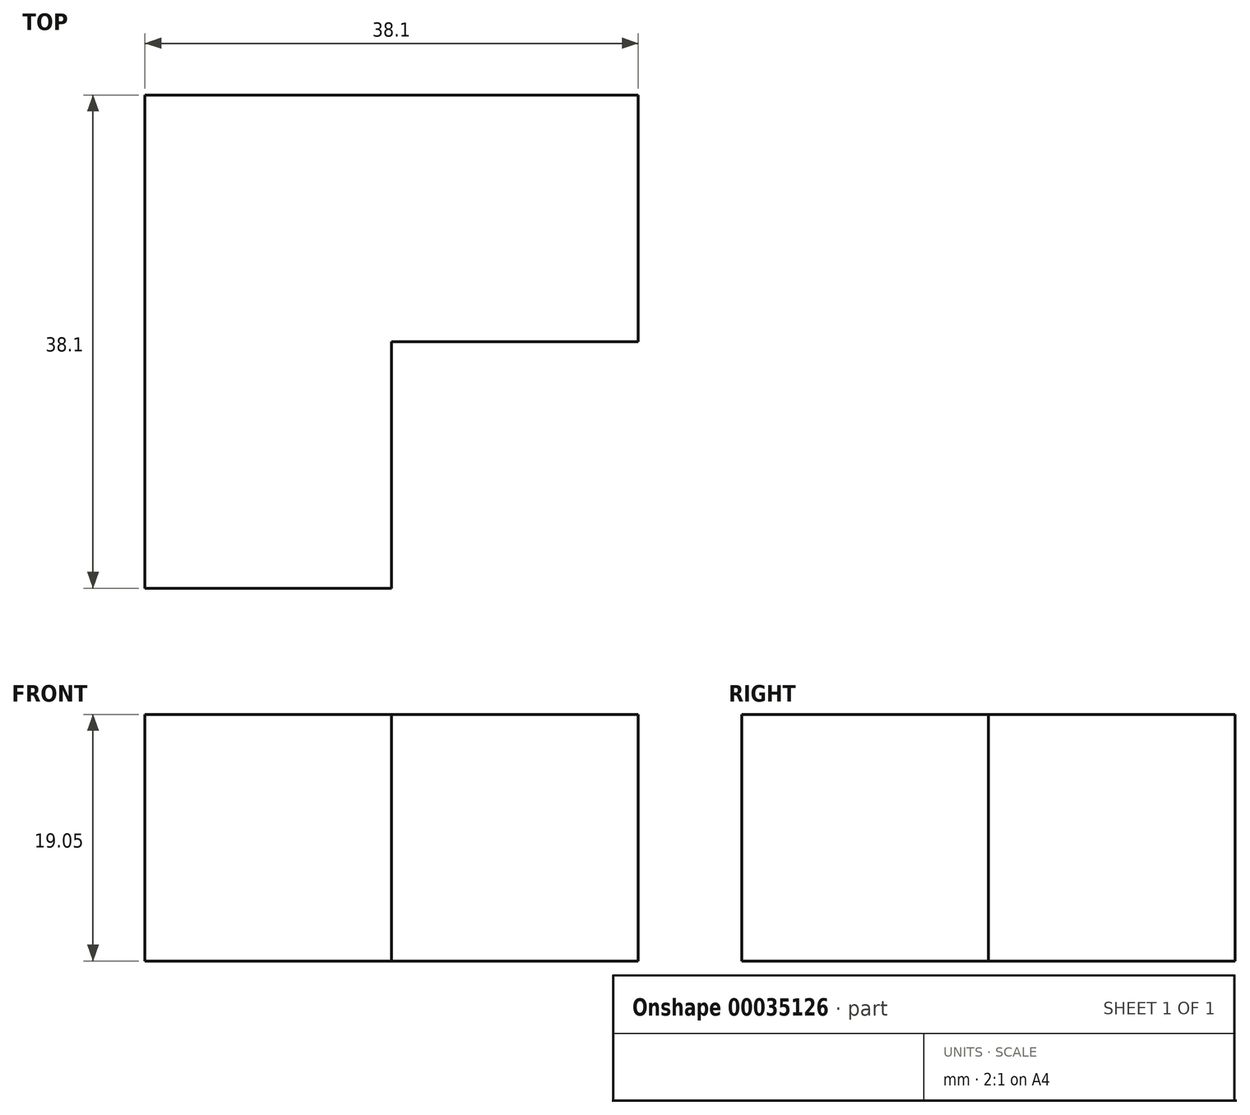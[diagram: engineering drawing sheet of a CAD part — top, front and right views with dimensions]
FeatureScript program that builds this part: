
annotation { "Feature Type Name" : "Feature", "Feature Type Description" : "" }
export const myFeature = defineFeature(function(context is Context, id is Id, definition is map)
    precondition{}
    {
        {
            var Q0;
            Q0=qCreatedBy(makeId("Top.planeOp"),FACE);
            var sketch = newSketch(context, id + "F0", { "sketchPlane" : qUnion([Q0])});
            skLineSegment(sketch, "E0.bottom", {"start": v(0, 0) * mm, "end": v(19.05, 0) * mm});
            skLineSegment(sketch, "E0.top", {"start": v(0, -19.05) * mm, "end": v(19.05, -19.05) * mm});
            skLineSegment(sketch, "E0.left", {"start": v(0, 0) * mm, "end": v(0, -19.05) * mm});
            skLineSegment(sketch, "E0.right", {"start": v(19.05, 0) * mm, "end": v(19.05, -19.05) * mm});
            skSolve(sketch);
        }
        {
            var Q0;
            Q0=makeQuery(id+"F0.imprint","IMPRINT",FACE,{"disambiguationData":[TD([[makeQuery(id+"F0.imprint","IMPRINT",EDGE,{"derivedFrom":sQuery(id+"F0.wireOp",EDGE,"E0.bottom")}),-1.0]])]});
            extrude(context, id + "F1", {"entities" : qUnion([Q0]), "depth" : 19.05 * mm});
        }
        {
            var Q0;
            Q0=makeQuery(id+"F1.opExtrude","SWEPT_FACE",FACE,{"disambiguationData":[OSD([sQuery(id+"F0.wireOp",EDGE,"E0.top")])]});
            var sketch = newSketch(context, id + "F2", { "sketchPlane" : qUnion([Q0])});
            skLineSegment(sketch, "E1.bottom", {"start": v(0, 19.05) * mm, "end": v(19.05, 19.05) * mm});
            skLineSegment(sketch, "E1.top", {"start": v(0, 0) * mm, "end": v(19.05, 0) * mm});
            skLineSegment(sketch, "E1.left", {"start": v(0, 19.05) * mm, "end": v(0, 0) * mm});
            skLineSegment(sketch, "E1.right", {"start": v(19.05, 19.05) * mm, "end": v(19.05, 0) * mm});
            skSolve(sketch);
        }
        {
            var Q0;
            Q0=makeQuery(id+"F2.imprint","IMPRINT",FACE,{"disambiguationData":[TD([[makeQuery(id+"F2.imprint","IMPRINT",EDGE,{"derivedFrom":sQuery(id+"F2.wireOp",EDGE,"E1.bottom")}),-1.0]])]});
            extrude(context, id + "F3", {"entities" : qUnion([Q0]), "operationType" : NewBodyOperationType.ADD, "depth" : 19.05 * mm});
        }
        {
            var Q0;
            Q0=makeQuery(id+"F3.boolean.opBoolean","MERGE",FACE,{"derivedFrom":[makeQuery(id+"F1.opExtrude","SWEPT_FACE",FACE,{"disambiguationData":[OSD([sQuery(id+"F0.wireOp",EDGE,"E0.right")])]}),makeQuery(id+"F3.opExtrude","SWEPT_FACE",FACE,{"disambiguationData":[OSD([sQuery(id+"F2.wireOp",EDGE,"E1.right")])]})]});
            var sketch = newSketch(context, id + "F4", { "sketchPlane" : qUnion([Q0])});
            skLineSegment(sketch, "E2.bottom", {"start": v(0, 19.05) * mm, "end": v(-19.05, 19.05) * mm});
            skLineSegment(sketch, "E2.top", {"start": v(0, 0) * mm, "end": v(-19.05, 0) * mm});
            skLineSegment(sketch, "E2.left", {"start": v(0, 19.05) * mm, "end": v(0, 0) * mm});
            skLineSegment(sketch, "E2.right", {"start": v(-19.05, 19.05) * mm, "end": v(-19.05, 0) * mm});
            skSolve(sketch);
        }
        {
            var Q0;
            Q0=makeQuery(id+"F4.imprint","IMPRINT",FACE,{"disambiguationData":[TD([[makeQuery(id+"F4.imprint","IMPRINT",EDGE,{"derivedFrom":sQuery(id+"F4.wireOp",EDGE,"E2.bottom")}),1.0]])]});
            extrude(context, id + "F5", {"entities" : qUnion([Q0]), "operationType" : NewBodyOperationType.ADD, "depth" : 19.05 * mm});
        }
    });
